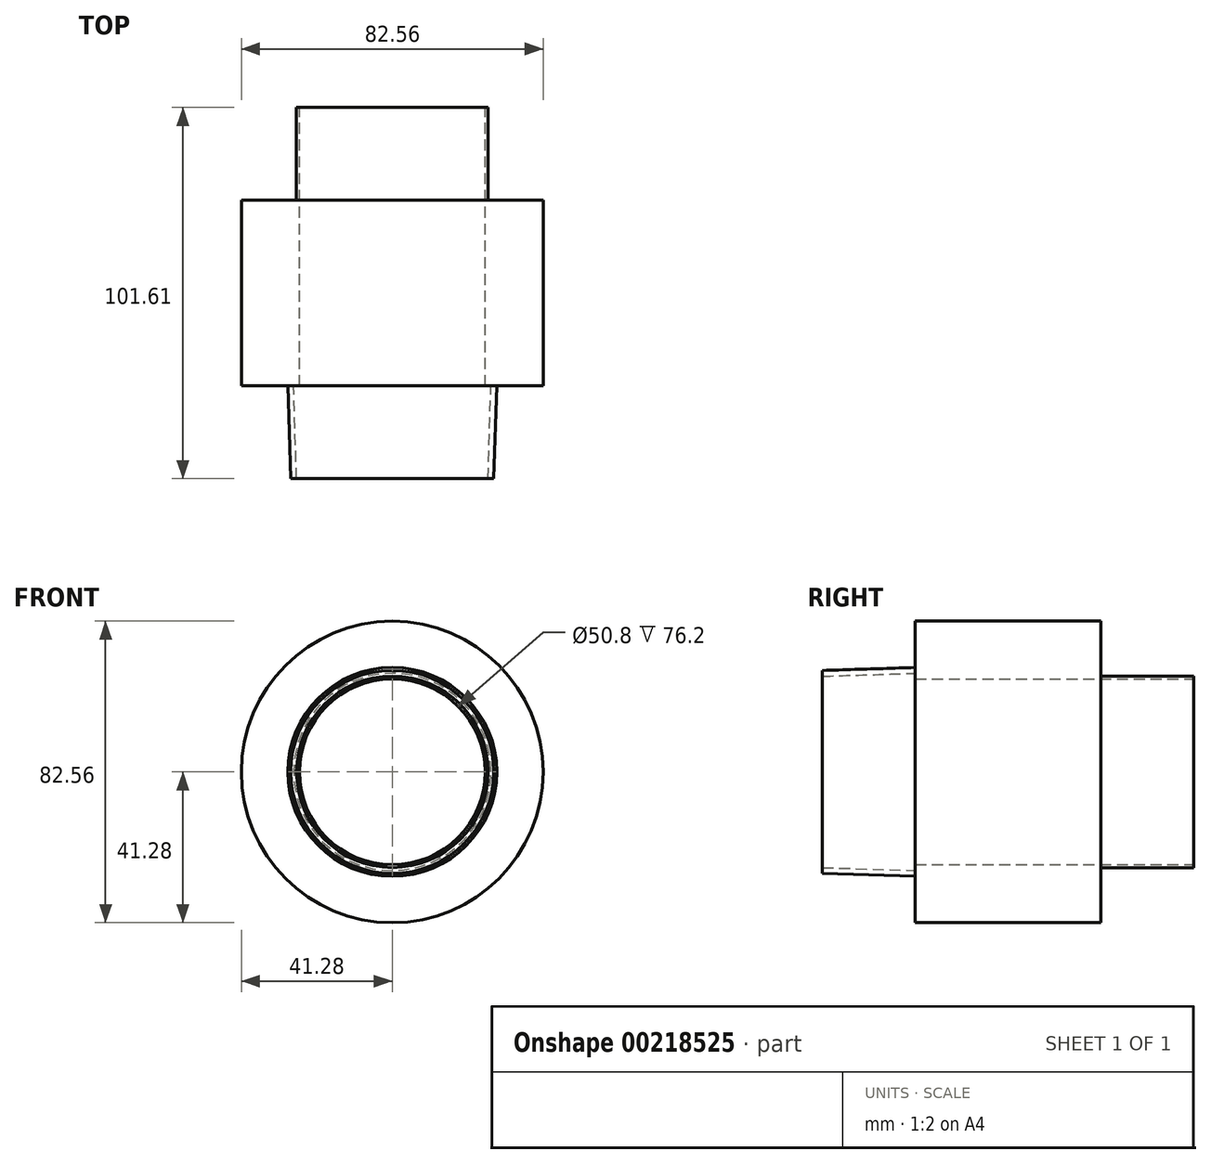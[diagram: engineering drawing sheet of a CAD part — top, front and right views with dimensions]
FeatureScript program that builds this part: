
annotation { "Feature Type Name" : "Feature", "Feature Type Description" : "" }
export const myFeature = defineFeature(function(context is Context, id is Id, definition is map)
    precondition{}
    {
        {
            var Q0;
            Q0=qCreatedBy(makeId("Front.planeOp"),FACE);
            var sketch = newSketch(context, id + "F0", { "sketchPlane" : qUnion([Q0])});
            skCircle(sketch, "E0", {"center": v(0, 0) * mm, "radius": 25.4 * mm});
            skCircle(sketch, "E1", {"center": v(0, 0) * mm, "radius": 26.2 * mm});
            skSolve(sketch);
        }
        {
            var Q0;
            Q0 = qSketchRegion(id + "F0", true);
            extrude(context, id + "F1", {"entities" : qUnion([Q0]), "depth" : 25.4 * mm});
        }
        {
            var Q0;
            Q0=makeQuery(id+"F1.opExtrude","CAP_FACE",FACE,{"disambiguationData":[OSD([sQuery(id+"F0.wireOp",EDGE,"E0"),sQuery(id+"F0.wireOp",EDGE,"E1")])],"isStart":false});
            var sketch = newSketch(context, id + "F2", { "sketchPlane" : qUnion([Q0])});
            skCircle(sketch, "E2", {"center": v(0, 0) * mm, "radius": 41.28 * mm});
            skSolve(sketch);
        }
        {
            var Q0;
            Q0 = qSketchRegion(id + "F2", true);
            extrude(context, id + "F3", {"entities" : qUnion([Q0]), "operationType" : NewBodyOperationType.ADD, "depth" : 50.8 * mm});
        }
        {
            var Q0;
            Q0=qCreatedBy(makeId("Right.planeOp"),FACE);
            var sketch = newSketch(context, id + "F4", { "sketchPlane" : qUnion([Q0])});
            skLineSegment(sketch, "E3", {"start": v(0, 0) * mm, "end": v(-76.2, 0) * mm});
            skPoint(sketch, "E4", {"position": v(-76.2, 28.57) * mm});
            skPoint(sketch, "E5", {"position": v(-101.6, 27.78) * mm});
            skLineSegment(sketch, "E6", {"start": v(-101.6, 27.78) * mm, "end": v(-76.2, 28.57) * mm});
            skPoint(sketch, "E7", {"position": v(-76.2, 26.99) * mm});
            skPoint(sketch, "E8", {"position": v(-101.6, 26.2) * mm});
            skLineSegment(sketch, "E9", {"start": v(-101.6, 26.2) * mm, "end": v(-76.2, 26.99) * mm});
            skLineSegment(sketch, "E10", {"start": v(-76.2, 28.57) * mm, "end": v(-76.2, 26.99) * mm});
            skLineSegment(sketch, "E11", {"start": v(-101.6, 27.78) * mm, "end": v(-101.6, 26.2) * mm});
            skSolve(sketch);
        }
        {
            var Q0;
            Q0=makeQuery(id+"F4.imprint","IMPRINT",FACE,{"disambiguationData":[TD([[makeQuery(id+"F4.imprint","IMPRINT",EDGE,{"derivedFrom":sQuery(id+"F4.wireOp",EDGE,"E6")}),-1.0]])]});
            var Q1;
            Q1=sQuery(id+"F4.wireOp",EDGE,"E3");
            revolve(context, id + "F5", {"operationType" : NewBodyOperationType.ADD, "entities" : qUnion([Q0]), "axis" : qUnion([Q1]), "revolveType" : RevolveType.FULL});
        }
        {
            var Q0;
            Q0=makeQuery(id+"F3.boolean.opBoolean","SPLIT",FACE,{"disambiguationData":[TD([makeQuery(id+"F1.opExtrude","SWEPT_FACE",FACE,{"disambiguationData":[OSD([sQuery(id+"F0.wireOp",EDGE,"E0")])]})])],"derivedFrom":makeQuery(id+"F3.opExtrude","CAP_FACE",FACE,{"disambiguationData":[OSD([sQuery(id+"F2.wireOp",EDGE,"E2")])],"isStart":true})});
            extrude(context, id + "F6", {"entities" : qUnion([Q0]), "operationType" : NewBodyOperationType.REMOVE, "oppositeDirection" : true, "depth" : 76.2 * mm});
        }
    });
